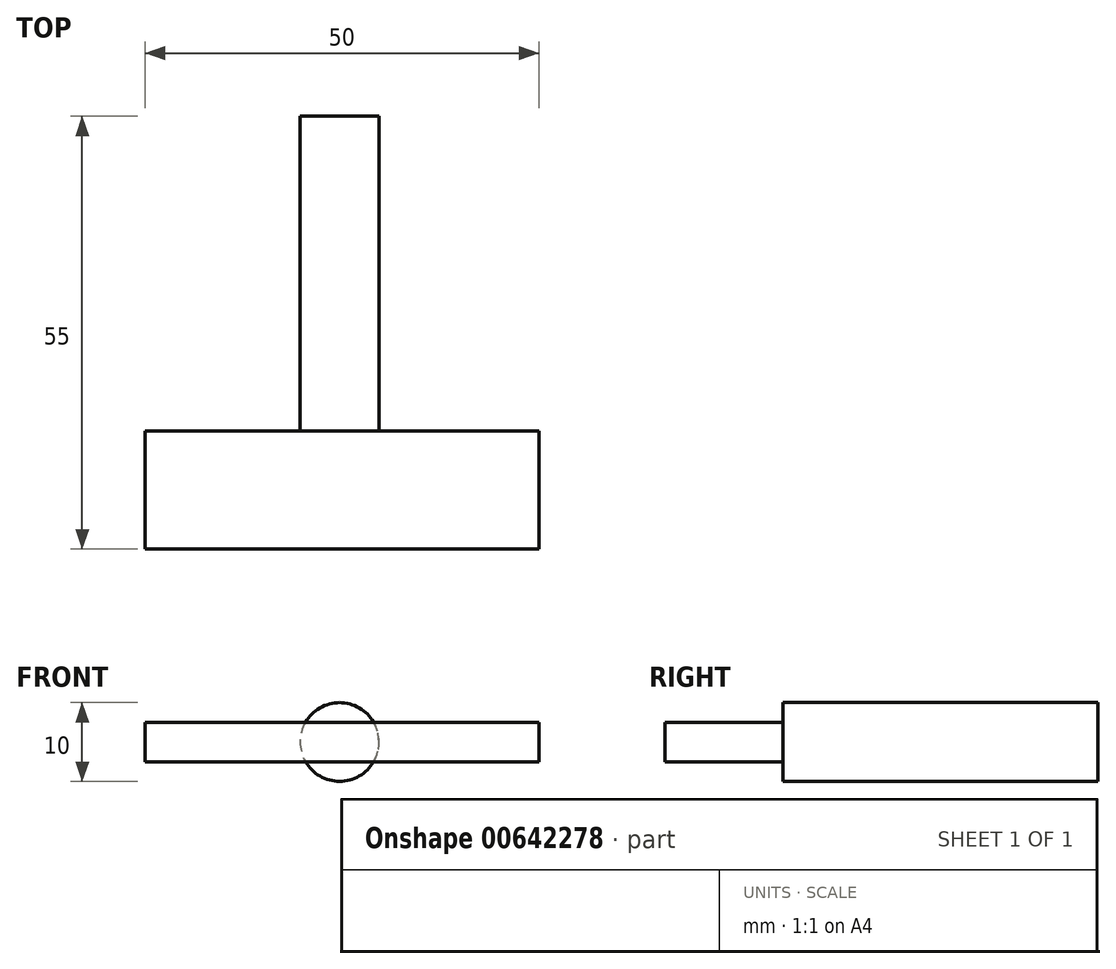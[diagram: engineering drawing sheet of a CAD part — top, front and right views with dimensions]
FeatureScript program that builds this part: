
annotation { "Feature Type Name" : "Feature", "Feature Type Description" : "" }
export const myFeature = defineFeature(function(context is Context, id is Id, definition is map)
    precondition{}
    {
        {
            var Q0;
            Q0=qCreatedBy(makeId("Front.planeOp"),FACE);
            var sketch = newSketch(context, id + "F0", { "sketchPlane" : qUnion([Q0])});
            skCircle(sketch, "E0", {"center": v(0, 0) * mm, "radius": 5 * mm});
            skSolve(sketch);
        }
        {
            var Q0;
            Q0=makeQuery(id+"F0.imprint","IMPRINT",FACE,{"disambiguationData":[TD([[makeQuery(id+"F0.imprint","IMPRINT",EDGE,{"derivedFrom":sQuery(id+"F0.wireOp",EDGE,"E0")}),1.0]])]});
            extrude(context, id + "F1", {"entities" : qUnion([Q0]), "depth" : 40 * mm, "offsetDistance" : 25 * mm});
        }
        {
            var Q0;
            Q0=qCreatedBy(makeId("Top.planeOp"),FACE);
            var sketch = newSketch(context, id + "F2", { "sketchPlane" : qUnion([Q0])});
            skLineSegment(sketch, "E1.bottom", {"start": v(25.32, -40) * mm, "end": v(-24.68, -40) * mm});
            skLineSegment(sketch, "E1.top", {"start": v(25.32, -55) * mm, "end": v(-24.68, -55) * mm});
            skLineSegment(sketch, "E1.left", {"start": v(25.32, -40) * mm, "end": v(25.32, -55) * mm});
            skLineSegment(sketch, "E1.right", {"start": v(-24.68, -40) * mm, "end": v(-24.68, -55) * mm});
            skSolve(sketch);
        }
        {
            var Q0;
            Q0=makeQuery(id+"F2.imprint","IMPRINT",FACE,{"disambiguationData":[TD([[makeQuery(id+"F2.imprint","IMPRINT",EDGE,{"derivedFrom":sQuery(id+"F2.wireOp",EDGE,"E1.bottom")}),1.0]])]});
            extrude(context, id + "F3", {"entities" : qUnion([Q0]), "operationType" : NewBodyOperationType.ADD, "endBound" : BoundingType.SYMMETRIC, "depth" : 5 * mm, "offsetDistance" : 25 * mm});
        }
    });
